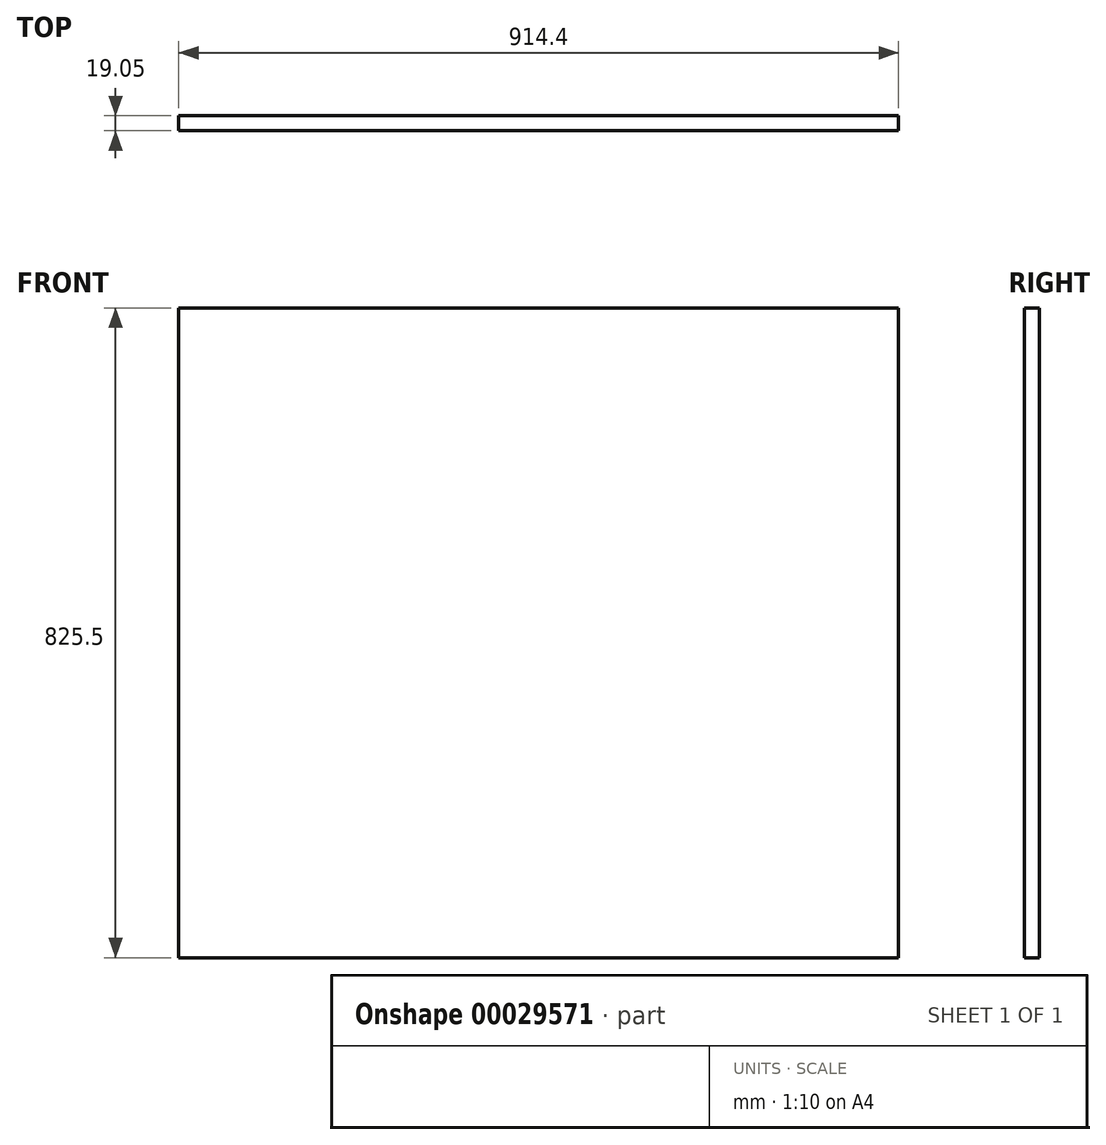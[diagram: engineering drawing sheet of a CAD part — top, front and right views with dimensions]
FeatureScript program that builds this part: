
annotation { "Feature Type Name" : "Feature", "Feature Type Description" : "" }
export const myFeature = defineFeature(function(context is Context, id is Id, definition is map)
    precondition{}
    {
        {
            var Q0;
            Q0=qCreatedBy(makeId("Front.planeOp"),FACE);
            var sketch = newSketch(context, id + "F0", { "sketchPlane" : qUnion([Q0])});
            skLineSegment(sketch, "E0.rect.bottom", {"start": v(457.2, 412.75) * mm, "end": v(-457.2, 412.75) * mm});
            skLineSegment(sketch, "E0.rect.top", {"start": v(457.2, -412.75) * mm, "end": v(-457.2, -412.75) * mm});
            skLineSegment(sketch, "E0.rect.left", {"start": v(457.2, 412.75) * mm, "end": v(457.2, -412.75) * mm});
            skLineSegment(sketch, "E0.rect.right", {"start": v(-457.2, 412.75) * mm, "end": v(-457.2, -412.75) * mm});
            skPoint(sketch, "E0.rect.middle", {"position": v(0, 0) * mm});
            skPoint(sketch, "E1", {"position": v(-393.7, 0) * mm});
            skSolve(sketch);
        }
        {
            var Q0;
            Q0 = qSketchRegion(id + "F0", true);
            extrude(context, id + "F1", {"entities" : qUnion([Q0]), "depth" : 19.05 * mm});
        }
    });
